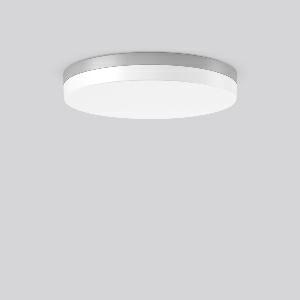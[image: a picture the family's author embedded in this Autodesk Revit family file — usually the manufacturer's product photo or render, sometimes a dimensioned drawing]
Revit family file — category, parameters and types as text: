
# Revit family: flat_slim_round_312633_004_6eee
name_source: partatom
category: Lighting Fixtures
units: mm (PartAtom-declared; Revit-internal decimal feet)

## family parameters
Cut with Voids When Loaded = No
Host = Face
Light Source = No
Part Type = Normal
Room Calculation Point = No
Round Connector Dimension = Use Diameter
Shared = No

## types (1)
- MultiLumen 1 830 (1 x LED Modul 830, 3350 lm, 3000)
    Apparent Load = 31 VA
    CIE Flux Codes = 41 71 90 86 100
    Color Rendering = 80
    Color Temperature = 3000
    Default Elevation = 1800 mm
    Height = 75 mm
    Lamp = 1 x LED Modul 830
    Lamp Light Flux = 3350 lm
    Lamp count = 1
    Length = 480 mm
    Lifetime = 50000 h
    Luminous efficacy = 108 lm/W
    Manufacturer = RZB
    ModVariant = No
    Model = 312633.004
    Mounting Place = Ceiling
    Mounting Type = Surface mounted
    Number of Poles = 1
    OnlyDefault = Yes
    Power Factor = 1
    Product Name = FLAT SLIM round
    Product group = Surface mounted ceiling and wall luminaires
    ProductGroupID = 305
    Protection Class = Protection class I
    Protection Degree = Degree of protection
    RLX_Detail_Level = 1
    RLX_Emergency_Light_Flux = 0 lm
    RLX_Emergency_Type = 0
    RLX_Emergency_Type_DB = No
    RlxData = <blob elided: 21665 chars, md5=6bf91b70>
    Socket = socket
    Standby Power = 0 W
    System Light Flux = 3350 lm
    System Power = 31 W
    Type Comments = MultiLumen 1 830
    Type Image = 312633.004.jpg
    URL = http://relux.com
    VarID = multilumen_1_830
    Voltage = 0 V
    Weight = 0.00 kg
    Width = 0 mm  [stored 0 ft]

note: [stored X ft] marks values corroborated as IEEE doubles in the binary element streams (Revit-internal decimal feet)

## geometry (parser evidence)
native form markers: Blend x4, Sweep x13
no freeform markers — native parametric forms only
